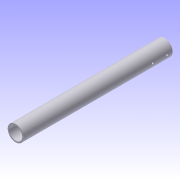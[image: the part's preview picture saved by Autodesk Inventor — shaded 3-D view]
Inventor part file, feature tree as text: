
AUTODESK INVENTOR PART (.ipt)
format: ipt  version: 2012 (Build 160160000, 160)  size: 98,304 bytes
history: native  units: in
note: dims shown in document units (in); Inventor stores cm internally (conversion verified against a paired STEP export)
features: extrude x3, sketch x2, plane x1, other x1, projected_geometry x1
ambient origin geometry x8: Origin, YZ Plane, XZ Plane, XY Plane, X Axis, Y Axis, Z Axis, Center Point
bodies: Solid1 (feature_tree)
feature tree (8):
  extrude  "Extrusion1"  Depth=1.656in
  plane  "Work Plane1"
  sketch  "Sketch2"  dims[d2=15.5in d3=0.0in d4=0.0in d5=0.5625in d6=1.5in d7=0.1875in d8=15.5in d9=0.0in d10=0.25in d11=0.25in d12=2.0in d13=1.25in d14=1.0in d15=0.0in]
  extrude  "Extrusion2"  TaperAngle=0.0deg  [1 undecoded]
  extrude  "Extrusion3"  Depth=0.5625in
  sketch  "Sketch1"  dims[d0=1.375in d1=1.656in]
  other  "Work Axis1"
  projected_geometry  "Projected Loop1"
note: 1 required parameter value undecoded (feature->parameter linkage not recoverable at this tier; creation-order binding heuristic only, values carry confidence <= 0.55)
